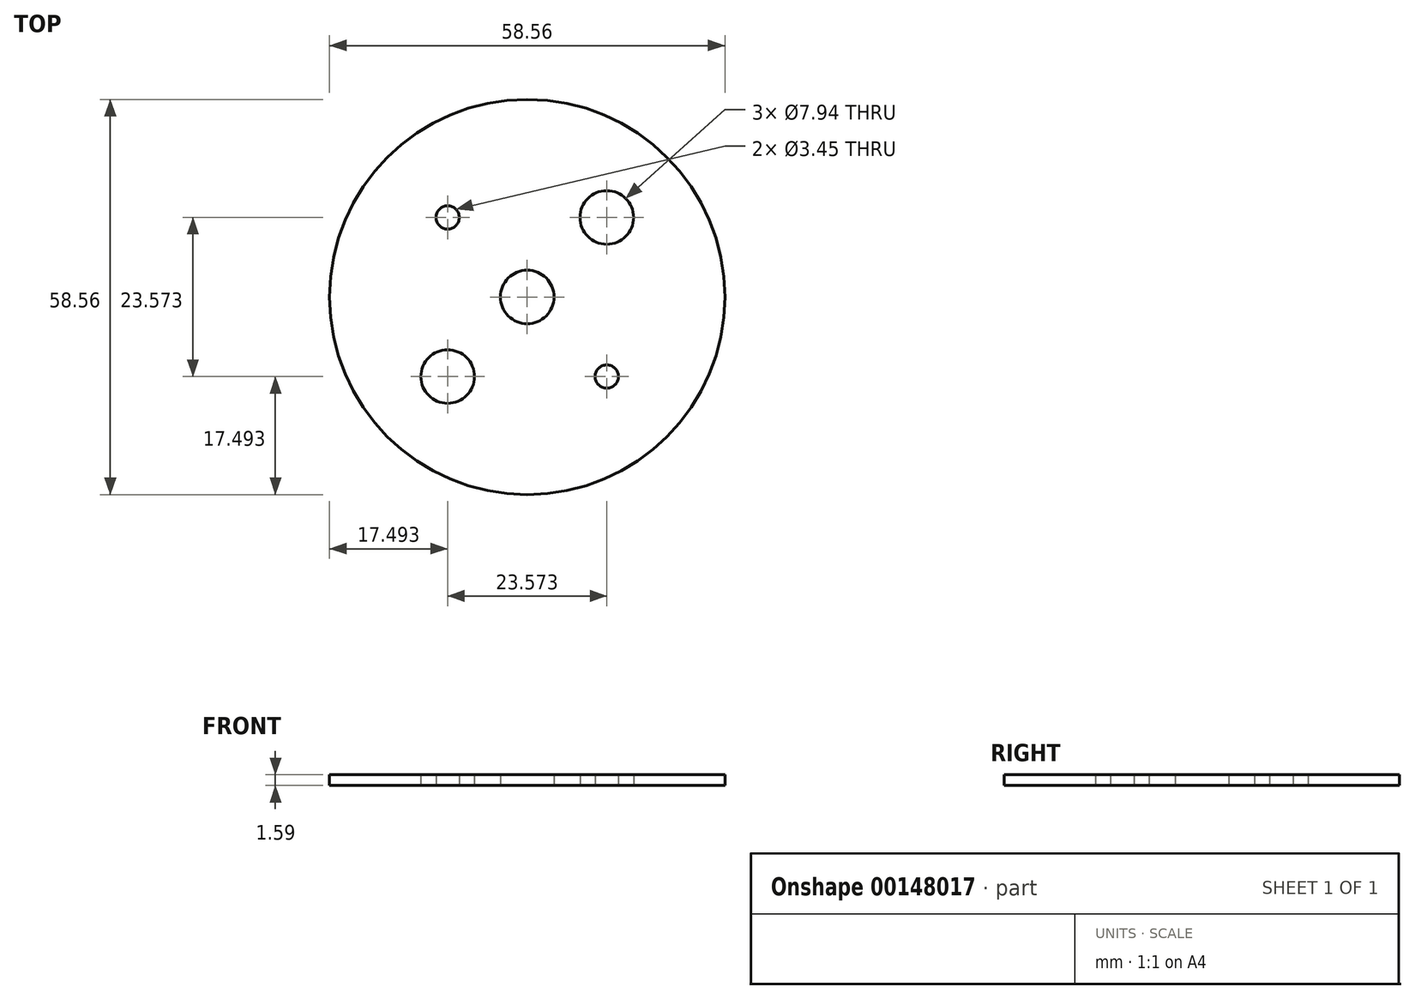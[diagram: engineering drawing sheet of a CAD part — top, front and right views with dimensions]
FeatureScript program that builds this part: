
annotation { "Feature Type Name" : "Feature", "Feature Type Description" : "" }
export const myFeature = defineFeature(function(context is Context, id is Id, definition is map)
    precondition{}
    {
        {
            var Q0;
            Q0=qCreatedBy(makeId("Top.planeOp"),FACE);
            var sketch = newSketch(context, id + "F0", { "sketchPlane" : qUnion([Q0])});
            skCircle(sketch, "E0", {"center": v(0, 0) * mm, "radius": 29.28 * mm});
            skCircle(sketch, "E1", {"center": v(0, 0) * mm, "radius": 3.97 * mm});
            skLineSegment(sketch, "E2.bottom", {"start": v(-11.79, 11.79) * mm, "end": v(11.79, 11.79) * mm, "construction": true});
            skLineSegment(sketch, "E2.top", {"start": v(-11.79, -11.79) * mm, "end": v(11.79, -11.79) * mm, "construction": true});
            skLineSegment(sketch, "E2.left", {"start": v(-11.79, 11.79) * mm, "end": v(-11.79, -11.79) * mm, "construction": true});
            skLineSegment(sketch, "E2.right", {"start": v(11.79, 11.79) * mm, "end": v(11.79, -11.79) * mm, "construction": true});
            skCircle(sketch, "E3", {"center": v(11.79, 11.79) * mm, "radius": 1.73 * mm, "construction": true});
            skCircle(sketch, "E4", {"center": v(-11.79, 11.79) * mm, "radius": 1.73 * mm});
            skCircle(sketch, "E5", {"center": v(-11.79, -11.79) * mm, "radius": 1.73 * mm, "construction": true});
            skCircle(sketch, "E6", {"center": v(11.79, -11.79) * mm, "radius": 1.73 * mm});
            skCircle(sketch, "E7", {"center": v(-11.79, -11.79) * mm, "radius": 3.97 * mm});
            skCircle(sketch, "E8", {"center": v(11.79, 11.79) * mm, "radius": 3.97 * mm});
            skSolve(sketch);
        }
        {
            var Q0;
            Q0=qSketchRegion(id+"F0",true);
            extrude(context, id + "F1", {"entities" : qUnion([Q0]), "depth" : 1.59 * mm});
        }
    });
